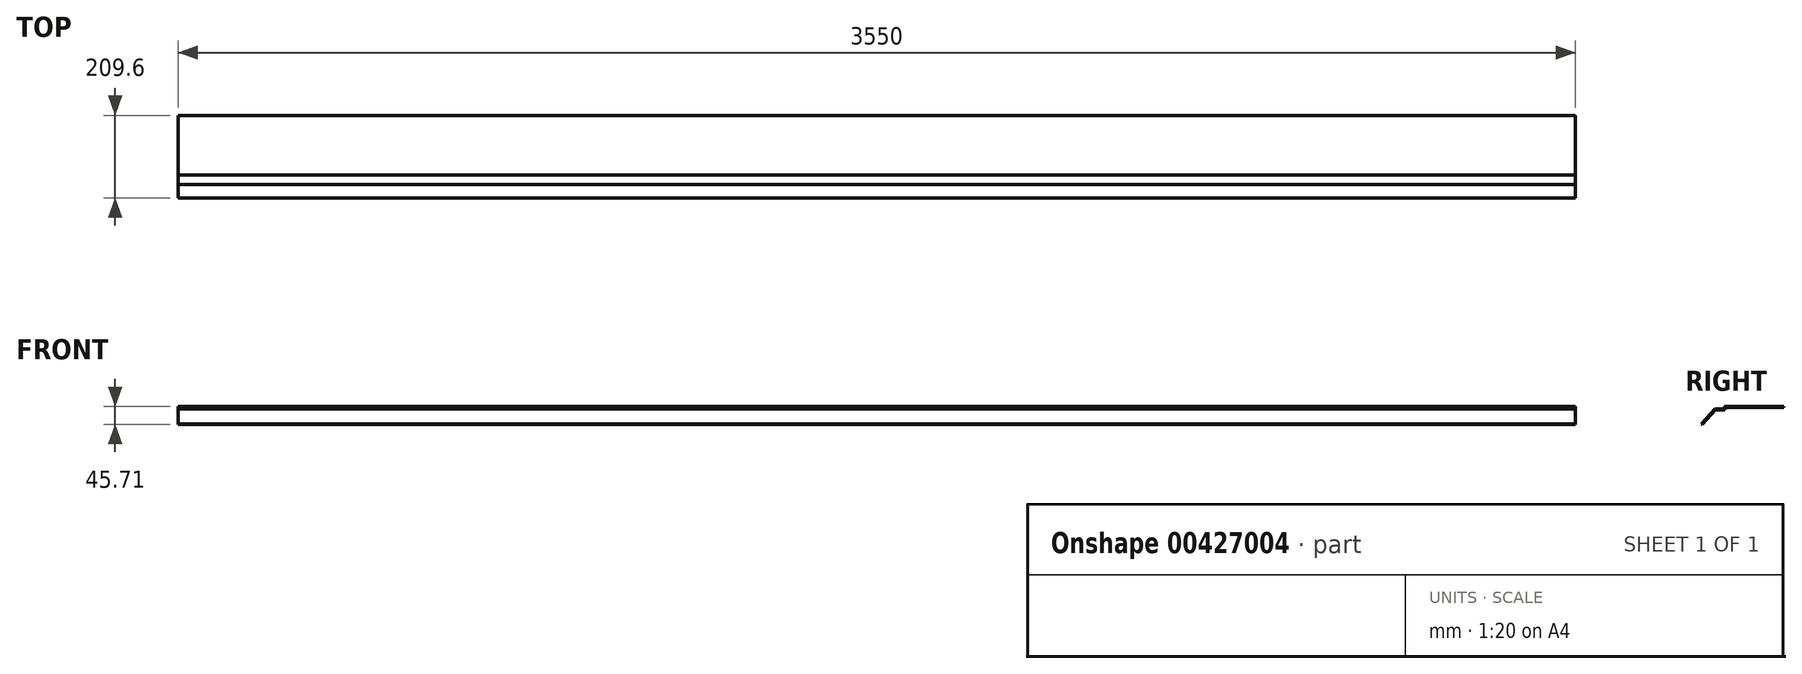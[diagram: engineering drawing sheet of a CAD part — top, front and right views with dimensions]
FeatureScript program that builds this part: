
annotation { "Feature Type Name" : "Feature", "Feature Type Description" : "" }
export const myFeature = defineFeature(function(context is Context, id is Id, definition is map)
    precondition{}
    {
        {
            var Q0;
            Q0=qCreatedBy(makeId("Right.planeOp"),FACE);
            var sketch = newSketch(context, id + "F0", { "sketchPlane" : qUnion([Q0])});
            skLineSegment(sketch, "E0", {"start": v(0, 0) * mm, "end": v(-150, 0) * mm});
            skLineSegment(sketch, "E1", {"start": v(-150, 0) * mm, "end": v(-150, -6.23) * mm});
            skLineSegment(sketch, "E2", {"start": v(-150, -6.23) * mm, "end": v(-175, -6.23) * mm});
            skLineSegment(sketch, "E3", {"start": v(-175, -6.23) * mm, "end": v(-208.1, -43.71) * mm});
            skLineSegment(sketch, "E4.0", {"start": v(-175.9, -4.23) * mm, "end": v(-209.6, -42.39) * mm});
            skLineSegment(sketch, "E4.1", {"start": v(-152, -4.23) * mm, "end": v(-175.9, -4.23) * mm});
            skLineSegment(sketch, "E4.2", {"start": v(-152, 2) * mm, "end": v(-152, -4.23) * mm});
            skLineSegment(sketch, "E4.3", {"start": v(0, 2) * mm, "end": v(-152, 2) * mm});
            skLineSegment(sketch, "E5", {"start": v(0, 0) * mm, "end": v(0, 2) * mm});
            skLineSegment(sketch, "E6", {"start": v(-208.1, -43.71) * mm, "end": v(-209.6, -42.39) * mm});
            skSolve(sketch);
        }
        {
            var Q0;
            Q0=makeQuery(id+"F0.imprint","IMPRINT",FACE,{"disambiguationData":[TD([[makeQuery(id+"F0.imprint","IMPRINT",EDGE,{"derivedFrom":sQuery(id+"F0.wireOp",EDGE,"E0")}),-1.0]])]});
            extrude(context, id + "F1", {"entities" : qUnion([Q0]), "depth" : 3550 * mm});
        }
    });
